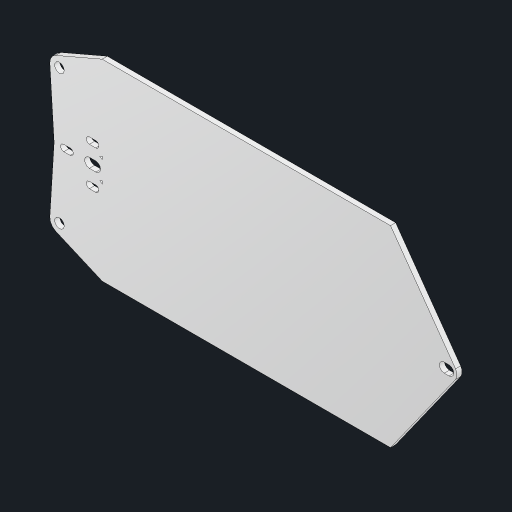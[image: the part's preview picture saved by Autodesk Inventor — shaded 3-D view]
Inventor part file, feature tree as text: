
AUTODESK INVENTOR PART (.ipt)
format: ipt  version: 2023.2 (Build 272271030, 271C)  size: 390,656 bytes
history: native  units: mm
features: extrude x4, sketch x3, projected_geometry x3, mirror x1, fillet x1
ambient origin geometry x8: Origin, YZ Plane, XZ Plane, XY Plane, X Axis, Y Axis, Z Axis, Center Point
bodies: Solid1 (feature_tree)
feature tree (12):
  extrude  "Extrusion1"  Depth=50.0mm
  extrude  "Extrusion2"  Depth=22.0mm
  extrude  "Extrusion3"  Depth=1.6mm
  mirror  "Mirror1"
  fillet  "Fillet2"  Radius=8.0mm
  extrude  "Extrusion4"  Depth=8.0mm
  sketch  "Sketch1"  dims[d0=90.0mm d1=50.0mm]
  projected_geometry  "Projected Loop1"
  sketch  "Sketch3"  dims[d2=5.0mm d3=22.0mm]
  projected_geometry  "Projected Loop2"
  sketch  "Sketch4"  dims[d5=36.0mm d6=132.0mm d7=8.0mm d8=8.0mm d9=4.0mm d10=3.0mm d11=3.0mm d12=8.0mm d13=3.0mm d14=1.5mm d15=8.5mm d16=1.25mm d17=5.0mm d18=5.0mm d19=1.0mm d20=3.0mm d21=16.0mm d22=12.0mm d23=1.0mm d24=1.0mm d25=1.0mm d26=2.0mm d27=1.0mm d28=2.0mm d29=2.0mm d30=2.0mm d31=2.0mm d32=2.0mm d33=1.0mm d34=5.0mm d35=5.0mm d36=5.0mm d37=1.5mm d38=1.5mm d39=1.6mm d40=0.0mm d42=5.0mm d43=1.6mm d44=0.0mm d45=3.0mm d46=3.0mm d47=3.0mm d48=3.0mm d50=0.0mm d51=0.0mm d52=2.0mm d54=3.0mm d55=3.0mm d56=3.0mm d57=3.0mm d58=3.0mm d59=3.0mm d60=3.0mm d61=32.331615mm d62=20.0mm d64=45.9mm d65=10.0mm d67=10.0mm d69=1.6mm d70=0.0mm]
  projected_geometry  "Projected Loop3"
